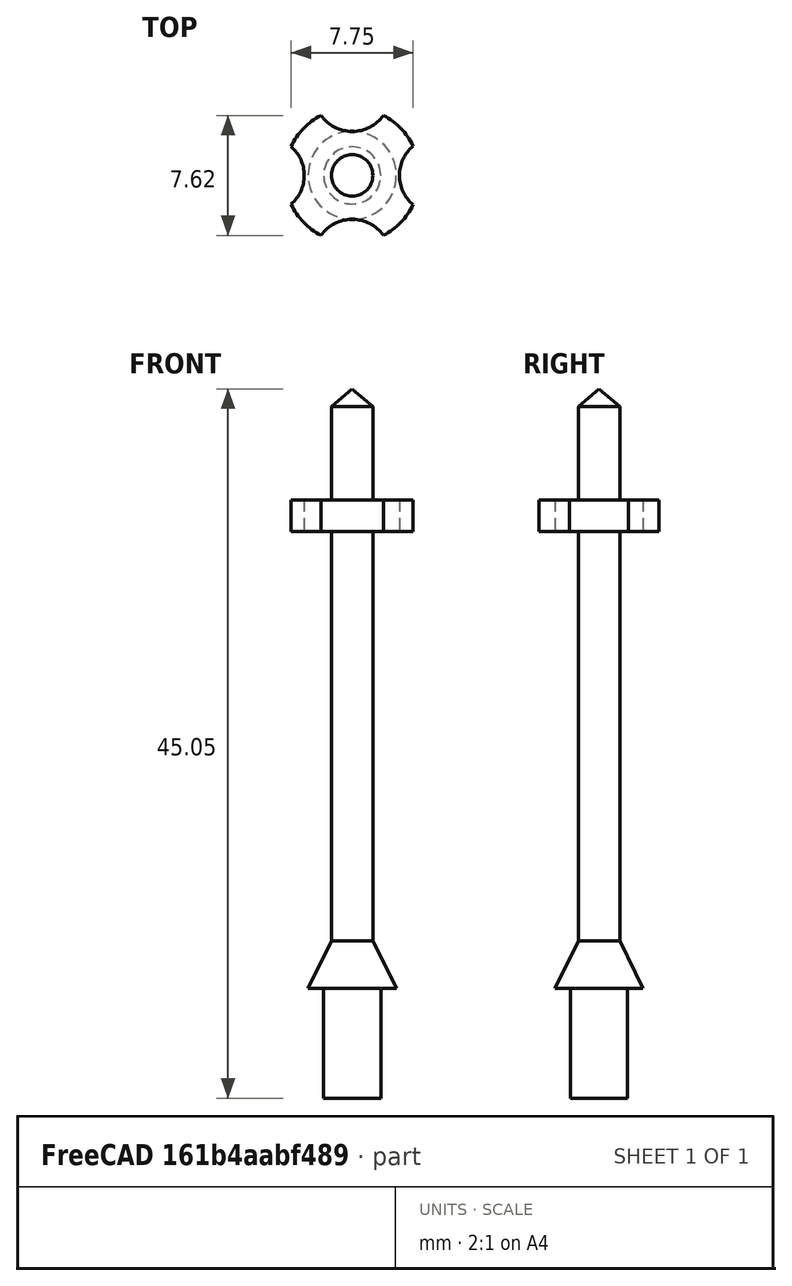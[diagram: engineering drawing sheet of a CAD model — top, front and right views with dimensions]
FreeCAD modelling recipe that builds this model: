
FCSTD DOCUMENT  (FreeCAD 0.19R23756 (Git))
Label: skis
License: All rights reserved
LicenseURL: http://en.wikipedia.org/wiki/All_rights_reserved
objects: Sketcher::SketchObject×2, Mesh::Feature×1, PartDesign::Revolution×1, PartDesign::Pad×1, PartDesign::Body×1
note: 7 computed .brp shape members not serialized (recipe doc carries the construction recipe); baked Part::Feature solids carry a one-line shape summary decoded from their .brp

FEATURE [Mesh::Feature] SkiStickAdult
FEATURE [Sketcher::SketchObject] Sketch
  FullyConstrained = false
  MapMode = 5
  Placement = pos=(0,0,0) rot=(0.57735,0.57735,0.57735;2.0944rad)
  Support = -> [YZ_Plane]
  sketch-geometry (7):
    g0: LineSegment StartX=0 StartY=0 StartZ=0 EndX=-1.81436 EndY=0 EndZ=0
    g1: LineSegment StartX=-1.81436 StartY=0 StartZ=0 EndX=-1.81436 EndY=6.96018 EndZ=0
    g2: LineSegment StartX=-1.81436 StartY=6.96018 StartZ=0 EndX=-2.79804 EndY=6.96018 EndZ=0
    g3: LineSegment StartX=-2.79804 StartY=6.96018 StartZ=0 EndX=-1.31094 EndY=9.97186 EndZ=0
    g4: LineSegment StartX=-1.31094 StartY=9.97186 StartZ=0 EndX=-1.31094 EndY=43.9283 EndZ=0
    g5: LineSegment StartX=-1.31094 StartY=43.9283 StartZ=0 EndX=0 EndY=45.0531 EndZ=0
    g6: LineSegment StartX=0 StartY=45.0531 StartZ=0 EndX=0 EndY=0 EndZ=0
  constraints (12):
    c: Coincident(g-1,g0)
    c: PointOnObject(g0,g-1)
    c: Coincident(g0,g1)
    c: Vertical(g1)
    c: Coincident(g1,g2)
    c: Horizontal(g2)
    c: Coincident(g2,g3)
    c: Coincident(g3,g4)
    c: Coincident(g4,g5)
    c: PointOnObject(g5,g-2)
    c: Coincident(g5,g6)
    c: Coincident(g6,g0)
FEATURE [PartDesign::Revolution] Revolution
  Angle = 360
  Axis = (-2e-16,3e-16,1)
  Base = (0,0,0)
  Placement = pos=(0,0,0) rot=(0.57735,0.57735,0.57735;2.0944rad)
  Profile = -> Sketch
  ReferenceAxis = -> Sketch [V_Axis]
FEATURE [Sketcher::SketchObject] Sketch001
  AttachmentOffset = pos=(0,0,36) rot=(0,0,1;0rad)
  FullyConstrained = false
  MapMode = 5
  Placement = pos=(0,0,36) rot=(0,0,1;0rad)
  Support = -> [XY_Plane]
  sketch-geometry (11):
    g0: ArcOfCircle CenterX=-5.48249 CenterY=0 CenterZ=0 NormalX=0 NormalY=0 NormalZ=1 AngleXU=0 Radius=2.43425 StartAngle=5.43014 EndAngle=7.13623
    g1: Circle CenterX=0 CenterY=0 CenterZ=0 NormalX=0 NormalY=0 NormalZ=1 AngleXU=0 Radius=4.29284
    g2: LineSegment StartX=-5.48249 StartY=0 StartZ=0 EndX=5.42852 EndY=0 EndZ=0
    g3: LineSegment StartX=0 StartY=5.22143 StartZ=0 EndX=0 EndY=-5.22143 EndZ=0
    g4: ArcOfCircle CenterX=0 CenterY=0 CenterZ=0 NormalX=0 NormalY=0 NormalZ=1 AngleXU=0 Radius=4.29284 StartAngle=2.05067 EndAngle=2.70025
    g5: ArcOfCircle CenterX=0 CenterY=5.22143 CenterZ=0 NormalX=0 NormalY=0 NormalZ=1 AngleXU=0 Radius=2.43425 StartAngle=3.76112 EndAngle=5.66366
    g6: ArcOfCircle CenterX=0 CenterY=0 CenterZ=0 NormalX=0 NormalY=0 NormalZ=1 AngleXU=0 Radius=4.29284 StartAngle=0.449796 EndAngle=1.09093
    g7: ArcOfCircle CenterX=5.42852 CenterY=0 CenterZ=0 NormalX=0 NormalY=0 NormalZ=1 AngleXU=0 Radius=2.43425 StartAngle=2.26784 EndAngle=4.01535
    g8: ArcOfCircle CenterX=0 CenterY=0 CenterZ=0 NormalX=0 NormalY=0 NormalZ=1 AngleXU=0 Radius=4.29284 StartAngle=5.19226 EndAngle=5.83339
    g9: ArcOfCircle CenterX=0 CenterY=-5.22143 CenterZ=0 NormalX=0 NormalY=0 NormalZ=1 AngleXU=0 Radius=2.43425 StartAngle=0.619527 EndAngle=2.52207
    g10: ArcOfCircle CenterX=0 CenterY=0 CenterZ=0 NormalX=0 NormalY=0 NormalZ=1 AngleXU=0 Radius=4.29284 StartAngle=3.58293 EndAngle=4.23252
  constraints (22):
    c: Coincident(g2,g0)
    c: Horizontal(g2)
    c: Coincident(g4,g0)
    c: PointOnObject(g4,g1)
    c: Coincident(g5,g3)
    c: Coincident(g5,g4)
    c: PointOnObject(g5,g1)
    c: Coincident(g6,g5)
    c: Coincident(g7,g2)
    c: Coincident(g7,g6)
    c: PointOnObject(g7,g1)
    c: Coincident(g8,g7)
    c: Coincident(g9,g3)
    c: Coincident(g9,g8)
    c: PointOnObject(g9,g1)
    c: Coincident(g10,g0)
    c: Coincident(g10,g9)
    c: Equal(g0,g5)
    c: Equal(g5,g7)
    c: Equal(g0,g9)
    c: Coincident(g10,g-1)
    c: Symmetric(g5,g9,g-1)
FEATURE [PartDesign::Pad] Pad
  BaseFeature = -> Revolution
  Direction = (1,1,1)
  Length = 2
  Length2 = 100
  Placement = pos=(0,0,0) rot=(0.57735,0.57735,0.57735;2.0944rad)
  Profile = -> Sketch001
  Type = 0
FEATURE [PartDesign::Body] Body
  Group = -> [Sketch,Revolution,Sketch001,Pad]
  Origin = -> Origin
  Tip = -> Pad
